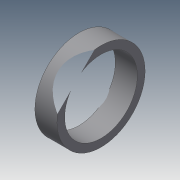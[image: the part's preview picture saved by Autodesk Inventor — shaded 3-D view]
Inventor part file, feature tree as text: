
AUTODESK INVENTOR PART (.ipt)
format: ipt  version: 2014 SP1 (Build 180222100, 222)  size: 242,688 bytes
history: native  units: in
note: dims shown in document units (in); Inventor stores cm internally (conversion verified against a paired STEP export)
features: extrude x4, sketch x3, pattern_circular x2
ambient origin geometry x8: Origin, YZ Plane, XZ Plane, XY Plane, X Axis, Y Axis, Z Axis, Center Point
bodies: Solid1 (feature_tree)
feature tree (9):
  extrude  "Extrusion1"  Depth=0.5in
  extrude  "Extrusion2"  Depth=1.5in
  extrude  "Extrusion3"  Depth=0.25in
  pattern_circular  "Circular Pattern1"  [2 undecoded]
  extrude  "Extrusion4"  Depth=0.25in
  pattern_circular  "Circular Pattern2"  [2 undecoded]
  sketch  "Sketch2"  dims[d0=4.0in d1=0.5in]
  sketch  "Sketch4"  dims[d2=0.77in d3=1.5in]
  sketch  "Sketch5"  dims[d4=2.0in d5=2.5in d6=3.0in d7=3.3in d17=0.25in d18=0.0in d19=4.0in d20=0.5in d21=0.77in d22=1.5in d23=2.0in d24=2.5in d25=3.0in d26=3.3in d27=0.14in d28=0.14in d29=0.14in d30=0.14in d31=0.14in d32=1.0in d33=0.0in d34=4.0in d35=0.5in d36=0.77in d37=1.5in d38=2.0in d39=2.5in d40=3.0in d41=3.3in d42=0.14in d43=0.14in d44=0.14in d45=0.14in d46=0.14in d47=0.25in d48=0.0in d49=3.1496in d50=360.0deg d53=0.0625in d54=0.25in d55=0.0in d56=3.1496in d57=360.0deg]
note: 4 required parameter values undecoded (feature->parameter linkage not recoverable at this tier; creation-order binding heuristic only, values carry confidence <= 0.55)
